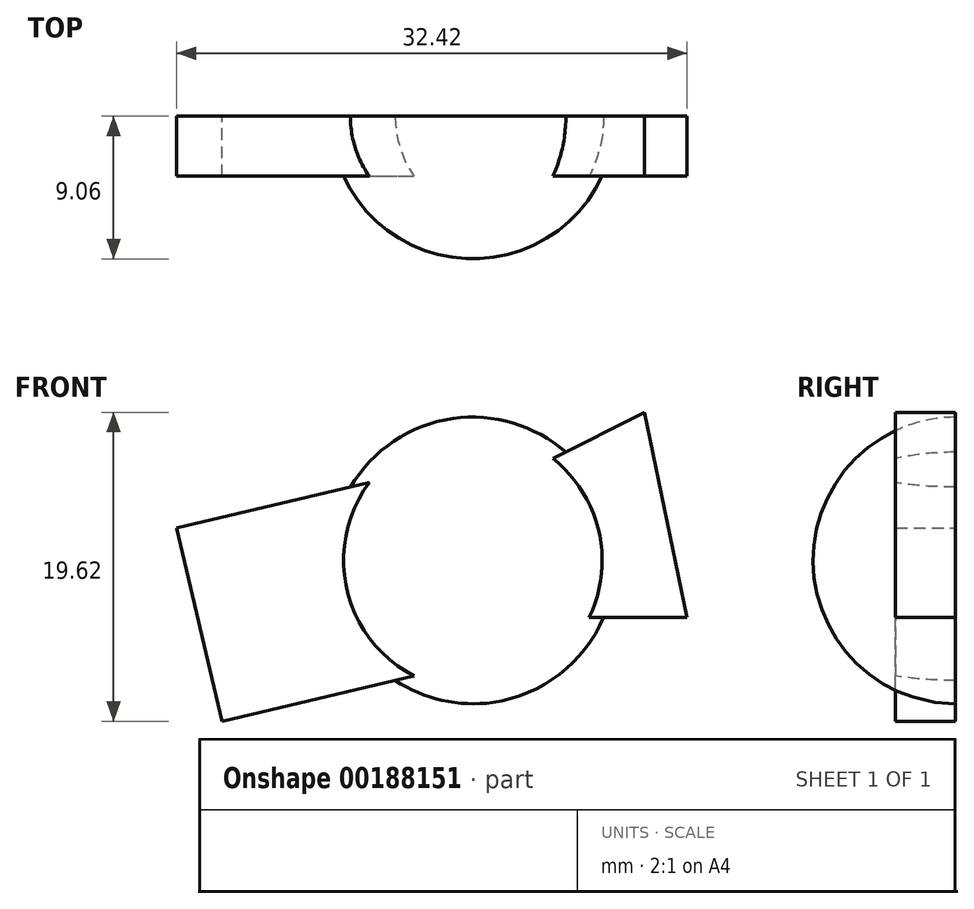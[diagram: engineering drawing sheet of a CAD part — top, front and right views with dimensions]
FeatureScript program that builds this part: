
annotation { "Feature Type Name" : "Feature", "Feature Type Description" : "" }
export const myFeature = defineFeature(function(context is Context, id is Id, definition is map)
    precondition{}
    {
        {
            var Q0;
            Q0=qCreatedBy(makeId("Front.planeOp"),FACE);
            var sketch = newSketch(context, id + "F0", { "sketchPlane" : qUnion([Q0])});
            skCircle(sketch, "E0", {"center": v(12.27, 10.2) * mm, "radius": 9.1 * mm});
            skPoint(sketch, "E0.first.point", {"position": v(11.06, 19.23) * mm});
            skPoint(sketch, "E0.second.point", {"position": v(13.6, 1.2) * mm});
            skPoint(sketch, "E0.third.point", {"position": v(20.92, 13.07) * mm});
            skLineSegment(sketch, "E1", {"start": v(23.24, 19.62) * mm, "end": v(25.93, 6.59) * mm});
            skPoint(sketch, "E2.end.orphan", {"position": v(-3.6, 0) * mm});
            skLineSegment(sketch, "E3", {"start": v(-3.6, 0) * mm, "end": v(-6.49, 12.27) * mm});
            skLineSegment(sketch, "E4", {"start": v(11.06, 19.23) * mm, "end": v(13.6, 1.2) * mm});
            skLineSegment(sketch, "E5", {"start": v(-6.49, 12.27) * mm, "end": v(6.13, 15.25) * mm});
            skLineSegment(sketch, "E6", {"start": v(-3.6, 0) * mm, "end": v(9.6, 3.12) * mm});
            skLineSegment(sketch, "E7", {"start": v(23.24, 19.62) * mm, "end": v(16.5, 16.22) * mm});
            skLineSegment(sketch, "E8", {"start": v(25.93, 6.59) * mm, "end": v(18.7, 6.59) * mm});
            skLineSegment(sketch, "E9", {"start": v(6.13, 15.25) * mm, "end": v(9.6, 3.12) * mm});
            skLineSegment(sketch, "E10", {"start": v(16.5, 16.22) * mm, "end": v(18.7, 6.59) * mm});
            skSolve(sketch);
        }
        {
            var Q0;
            {var subQ2=sQuery(id+"F0.wireOp",EDGE,"E4");Q0=makeQuery(id+"F0.imprint","IMPRINT",FACE,{"disambiguationData":[TD([[makeQuery(id+"F0.imprint","IMPRINT",EDGE,{"derivedFrom":subQ2}),1.0]])]});}
            var Q1;
            {var subQ5=sQuery(id+"F0.wireOp",EDGE,"E10");Q1=makeQuery(id+"F0.imprint","IMPRINT",FACE,{"disambiguationData":[TD([[makeQuery(id+"F0.imprint","IMPRINT",EDGE,{"derivedFrom":subQ5}),1.0]])]});}
            var Q2;
            Q2=sQuery(id+"F0.wireOp",EDGE,"E4");
            revolve(context, id + "F1", {"entities" : qUnion([Q0, Q1]), "axis" : qUnion([Q2]), "revolveType" : RevolveType.ONE_DIRECTION, "angle" : 180 * degree});
        }
        {
            var Q0;
            {var subQ5=sQuery(id+"F0.wireOp",EDGE,"E9");Q0=makeQuery(id+"F0.imprint","IMPRINT",FACE,{"disambiguationData":[TD([[makeQuery(id+"F0.imprint","IMPRINT",EDGE,{"derivedFrom":subQ5}),-1.0]])]});}
            var Q1;
            {var subQ5=sQuery(id+"F0.wireOp",EDGE,"E3");Q1=makeQuery(id+"F0.imprint","IMPRINT",FACE,{"disambiguationData":[TD([[makeQuery(id+"F0.imprint","IMPRINT",EDGE,{"derivedFrom":subQ5}),-1.0]])]});}
            var Q2;
            {var subQ5=sQuery(id+"F0.wireOp",EDGE,"E1");Q2=makeQuery(id+"F0.imprint","IMPRINT",FACE,{"disambiguationData":[TD([[makeQuery(id+"F0.imprint","IMPRINT",EDGE,{"derivedFrom":subQ5}),-1.0]])]});}
            var Q3;
            {var subQ5=sQuery(id+"F0.wireOp",EDGE,"E10");Q3=makeQuery(id+"F0.imprint","IMPRINT",FACE,{"disambiguationData":[TD([[makeQuery(id+"F0.imprint","IMPRINT",EDGE,{"derivedFrom":subQ5}),1.0]])]});}
            extrude(context, id + "F2", {"entities" : qUnion([Q0, Q1, Q2, Q3]), "operationType" : NewBodyOperationType.ADD, "depth" : 3.8 * mm});
        }
    });
